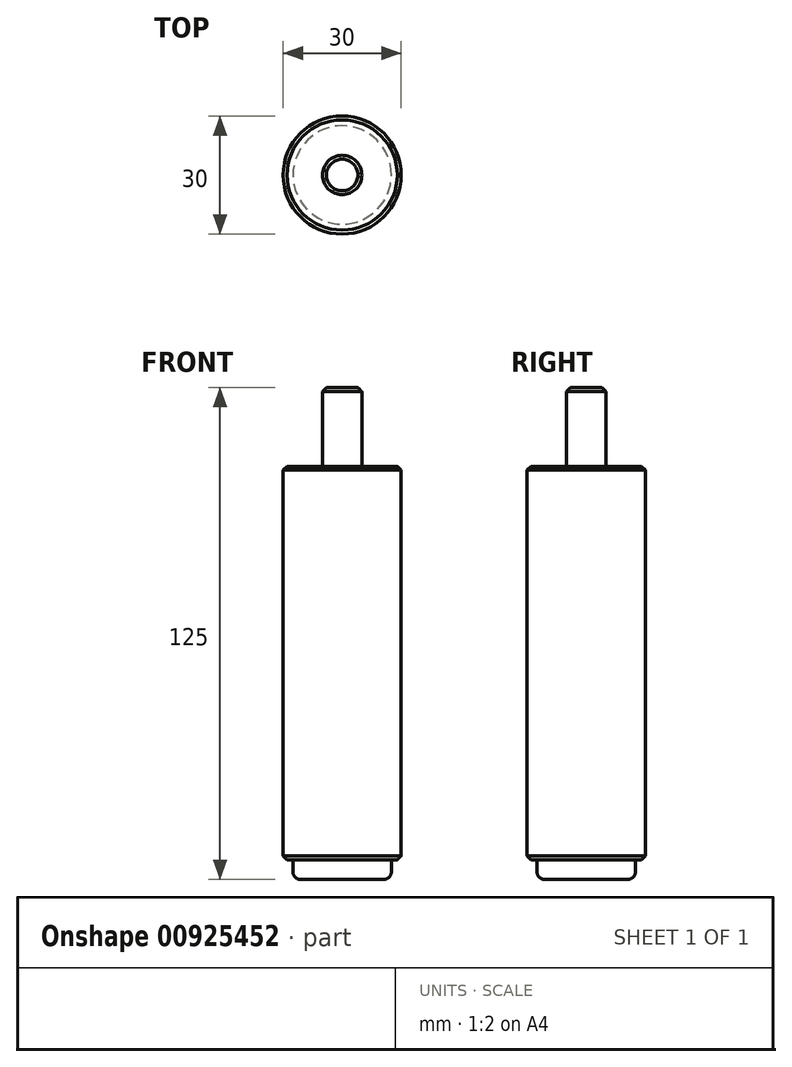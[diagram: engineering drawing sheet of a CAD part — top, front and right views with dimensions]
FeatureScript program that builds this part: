
annotation { "Feature Type Name" : "Feature", "Feature Type Description" : "" }
export const myFeature = defineFeature(function(context is Context, id is Id, definition is map)
    precondition{}
    {
        {
            var Q0;
            Q0=qCreatedBy(makeId("Top.planeOp"),FACE);
            var sketch = newSketch(context, id + "F0", { "sketchPlane" : qUnion([Q0])});
            skCircle(sketch, "E0", {"center": v(0, 0) * mm, "radius": 12.5 * mm});
            skSolve(sketch);
        }
        {
            var Q0;
            Q0=makeQuery(id+"F0.imprint","IMPRINT",FACE,{"disambiguationData":[TD([[makeQuery(id+"F0.imprint","IMPRINT",EDGE,{"derivedFrom":sQuery(id+"F0.wireOp",EDGE,"E0")}),1.0]])]});
            extrude(context, id + "F1", {"entities" : qUnion([Q0]), "depth" : 20 * mm, "offsetDistance" : 25 * mm});
        }
        {
            var Q0;
            Q0=qCreatedBy(makeId("Top.planeOp"),FACE);
            cPlane(context, id + "F2", {"entities" : qUnion([Q0]), "cplaneType" : CPlaneType.OFFSET, "offset" : 5 * mm, "width" : 150 * mm, "height" : 150 * mm});
        }
        {
            var Q0;
            Q0=qCreatedBy(id+"F2.planeOp",FACE);
            var sketch = newSketch(context, id + "F3", { "sketchPlane" : qUnion([Q0])});
            skCircle(sketch, "E1", {"center": v(0, 0) * mm, "radius": 15 * mm});
            skSolve(sketch);
        }
        {
            var Q0;
            Q0=makeQuery(id+"F3.imprint","IMPRINT",FACE,{"disambiguationData":[TD([[makeQuery(id+"F3.imprint","IMPRINT",EDGE,{"derivedFrom":sQuery(id+"F3.wireOp",EDGE,"E1")}),1.0]])]});
            var Q1;
            Q1=sQuery(id+"F3.wireOp",EDGE,"E1");
            extrude(context, id + "F4", {"entities" : qUnion([Q0]), "operationType" : NewBodyOperationType.ADD, "surfaceEntities" : qUnion([Q1]), "depth" : 100 * mm, "offsetDistance" : 25 * mm});
        }
        {
            var Q0;
            Q0=makeQuery(id+"F4.opExtrude","CAP_EDGE",EDGE,{"disambiguationData":[OSD([sQuery(id+"F3.wireOp",EDGE,"E1")])],"isStart":true});
            chamfer(context, id + "F5", {"entities" : qUnion([Q0]), "width" : 1 * mm, "tangentPropagation" : true});
        }
        {
            var Q0;
            Q0=makeQuery(id+"F4.opExtrude","CAP_EDGE",EDGE,{"disambiguationData":[OSD([sQuery(id+"F3.wireOp",EDGE,"E1")])],"isStart":false});
            chamfer(context, id + "F6", {"entities" : qUnion([Q0]), "width" : 1 * mm, "tangentPropagation" : true});
        }
        {
            var Q0;
            Q0=makeQuery(id+"F4.opExtrude","CAP_FACE",FACE,{"disambiguationData":[OSD([sQuery(id+"F3.wireOp",EDGE,"E1")])],"isStart":false});
            var sketch = newSketch(context, id + "F7", { "sketchPlane" : qUnion([Q0])});
            skCircle(sketch, "E2", {"center": v(0, 0) * mm, "radius": 5 * mm});
            skSolve(sketch);
        }
        {
            var Q0;
            Q0=makeQuery(id+"F7.imprint","IMPRINT",FACE,{"disambiguationData":[TD([[makeQuery(id+"F7.imprint","IMPRINT",EDGE,{"derivedFrom":sQuery(id+"F7.wireOp",EDGE,"E2")}),1.0]])]});
            var Q1;
            Q1=sQuery(id+"F7.wireOp",EDGE,"E2");
            extrude(context, id + "F8", {"entities" : qUnion([Q0]), "operationType" : NewBodyOperationType.ADD, "surfaceEntities" : qUnion([Q1]), "depth" : 20 * mm, "offsetDistance" : 25 * mm});
        }
        {
            var Q0;
            Q0=makeQuery(id+"F8.opExtrude","CAP_EDGE",EDGE,{"disambiguationData":[OSD([sQuery(id+"F7.wireOp",EDGE,"E2")])],"isStart":false});
            chamfer(context, id + "F9", {"entities" : qUnion([Q0]), "width" : 1 * mm, "tangentPropagation" : true});
        }
        {
            var Q0;
            Q0=makeQuery(id+"F1.opExtrude","CAP_EDGE",EDGE,{"disambiguationData":[OSD([sQuery(id+"F0.wireOp",EDGE,"E0")])],"isStart":true});
            fillet(context, id + "F10", {"entities" : qUnion([Q0]), "radius" : 2 * mm, "tangentPropagation" : true, "allowEdgeOverflow" : false});
        }
    });
